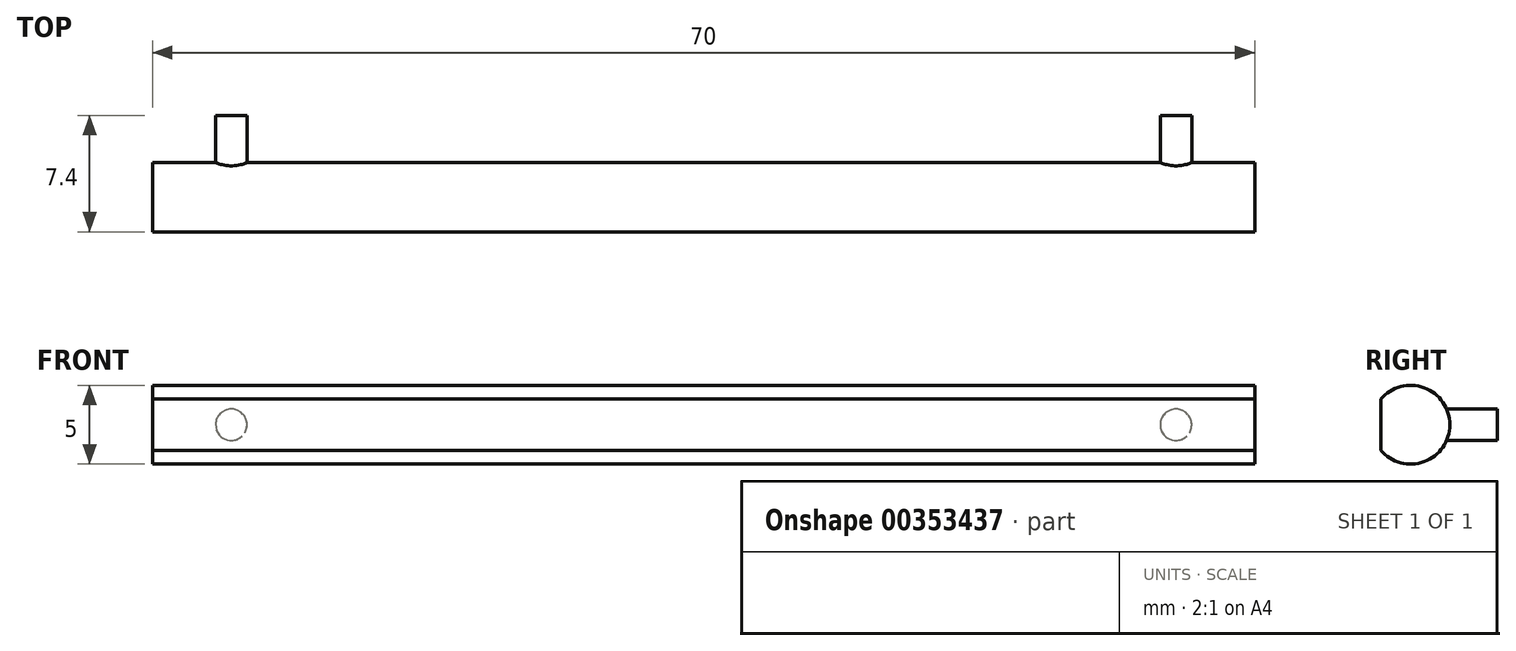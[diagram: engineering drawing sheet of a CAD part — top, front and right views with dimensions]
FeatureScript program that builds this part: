
annotation { "Feature Type Name" : "Feature", "Feature Type Description" : "" }
export const myFeature = defineFeature(function(context is Context, id is Id, definition is map)
    precondition{}
    {
        {
            var Q0;
            Q0=qCreatedBy(makeId("Right.planeOp"),FACE);
            var sketch = newSketch(context, id + "F0", { "sketchPlane" : qUnion([Q0])});
            skCircle(sketch, "E0", {"center": v(0, 0) * mm, "radius": 2.5 * mm});
            skSolve(sketch);
        }
        {
            var Q0;
            Q0=makeQuery(id+"F0.imprint","IMPRINT",FACE,{"disambiguationData":[TD([[makeQuery(id+"F0.imprint","IMPRINT",EDGE,{"derivedFrom":sQuery(id+"F0.wireOp",EDGE,"E0")}),1.0]])]});
            extrude(context, id + "F1", {"entities" : qUnion([Q0]), "endBound" : BoundingType.SYMMETRIC, "depth" : 70 * mm});
        }
        {
            var Q0;
            Q0=qCreatedBy(makeId("Front.planeOp"),FACE);
            var sketch = newSketch(context, id + "F2", { "sketchPlane" : qUnion([Q0])});
            skCircle(sketch, "E1", {"center": v(-30, 0) * mm, "radius": 1 * mm});
            skCircle(sketch, "E2", {"center": v(30, 0) * mm, "radius": 1 * mm});
            skSolve(sketch);
        }
        {
            var Q0;
            Q0 = qSketchRegion(id + "F2", true);
            extrude(context, id + "F3", {"entities" : qUnion([Q0]), "operationType" : NewBodyOperationType.ADD, "oppositeDirection" : true, "depth" : 5.5 * mm});
        }
        {
            var Q0;
            Q0=makeQuery(id+"F1.opExtrude","CAP_FACE",FACE,{"disambiguationData":[OSD([sQuery(id+"F0.wireOp",EDGE,"E0")])],"isStart":false});
            var sketch = newSketch(context, id + "F4", { "sketchPlane" : qUnion([Q0])});
            skLineSegment(sketch, "E3.bottom", {"start": v(-1.9, 2.13) * mm, "end": v(-4.06, 2.13) * mm});
            skLineSegment(sketch, "E3.top", {"start": v(-1.9, -2.13) * mm, "end": v(-4.06, -2.13) * mm});
            skLineSegment(sketch, "E3.left", {"start": v(-1.9, 2.13) * mm, "end": v(-1.9, -2.13) * mm});
            skLineSegment(sketch, "E3.right", {"start": v(-4.06, 2.13) * mm, "end": v(-4.06, -2.13) * mm});
            skPoint(sketch, "E3.middle", {"position": v(-2.98, 0) * mm});
            skSolve(sketch);
        }
        {
            var Q0;
            {var subQ0=sQuery(id+"F4.wireOp",EDGE,"E3.left");var subQ1=makeQuery(id+"F1.opExtrude","CAP_EDGE",EDGE,{"disambiguationData":[OSD([sQuery(id+"F0.wireOp",EDGE,"E0")])],"isStart":false});var subQ2=makeQuery(id+"F4.imprint","INTERSECT",VERTEX,{"disambiguationData":[OD(0.0)],"derivedFrom":[subQ1,subQ0]});Q0=makeQuery(id+"F4.imprint","IMPRINT",FACE,{"disambiguationData":[TD([[makeQuery(id+"F4.imprint","IMPRINT",EDGE,{"disambiguationData":[TD([[subQ2,-1.0]])],"derivedFrom":subQ0}),-1.0]])]});}
            extrude(context, id + "F5", {"entities" : qUnion([Q0]), "operationType" : NewBodyOperationType.REMOVE, "endBound" : BoundingType.THROUGH_ALL, "oppositeDirection" : true, "depth" : 25 * mm});
        }
    });
